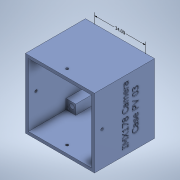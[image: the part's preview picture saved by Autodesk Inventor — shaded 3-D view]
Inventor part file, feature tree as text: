
AUTODESK INVENTOR PART (.ipt)
format: ipt  version: 2022.1 (Build 261234000, 234)  size: 864,256 bytes
history: native  units: mm
features: sketch x6, other x5, hole x3, reference x3, extrude x2, emboss x1
ambient origin geometry x8: Origin, YZ Plane, XZ Plane, XY Plane, X Axis, Y Axis, Z Axis, Center Point
bodies: Solid5 (feature_tree)
feature tree (20):
  other  "Annotations"
  extrude  "Extrusion9"  Depth=34.0mm
  extrude  "Extrusion10"  Depth=42.0mm
  emboss  "Emboss2"
  hole  "Hole1"  [1 undecoded]
  hole  "Hole2"  [1 undecoded]
  hole  "Hole3"  [1 undecoded]
  sketch  "Sketch8"  dims[d46=34.0mm d47=34.0mm]
  sketch  "Sketch9"  dims[d48=3.0mm d49=42.0mm]
  sketch  "Sketch10"  dims[d50=42.0mm d51=2.0mm]
  sketch  "Sketch11"  dims[d52=2.0mm d53=29.0mm]
  sketch  "Sketch12"  dims[d54=29.0mm d55=15.0mm d56=0.0mm]
  reference  "Reference1"
  reference  "Reference2"
  sketch  "Sketch13"  dims[d57=25.0mm d58=0.0mm d59=1.0mm d60=0.0mm d61=39.0mm d62=39.0mm d63=1.69418mm d64=4.369mm d65=3.023mm d66=2.0mm d67=14.3117mm d68=8.0mm d69=20.594885mm d70=1.69418mm d71=4.369mm d72=4.369mm d73=2.0mm d74=14.3117mm d75=8.0mm d76=20.594885mm d77=1.69418mm d78=4.369mm d79=4.0mm d80=2.0mm d81=90.0deg d82=8.0mm d83=20.594885mm d86=34.0mm]
  reference  "Reference3"
  parser-record x1  (decoder bookkeeping rows leaked as tree rows — omitted from the tree; the rows remain in map.json)
  other  "IMX178 Camera Case Assembly.iam"
  other  "IMX178 Camera Case Cap:1"
  other  "Linear Dimension 1"
note: 3 required parameter values undecoded (feature->parameter linkage not recoverable at this tier; creation-order binding heuristic only, values carry confidence <= 0.55)
note: 1 file-system path scrubbed to <path> (originals preserved in map.json)
